# Revit family: Nuaire_IfcFanType_Svtc100
name_source: partatom
category: Mechanical Equipment
revit_build: Autodesk Revit 2018 (Build: 20170223_1515(x64)
units: mm (PartAtom-declared; Revit-internal decimal feet)

## family parameters
Always vertical = No
Cut with Voids When Loaded = No
OmniClass Number = 23.75.00.00
OmniClass Title = Climate Control (HVAC)
Part Type = Normal
Room Calculation Point = No
Round Connector Dimension = Use Diameter
Shared = No
Work Plane-Based = No

## types (4) — shared parameters
6 Monthly = SFG20 20-03
Access Clearance Left = 600 mm
Annually = SFG20 20-03
BMS Links = No
Battery Supply = No
CE Approval = Yes
COBie.Type = Yes
COBie.Type.Category = Pr_65_67_29_12 : Centrifugal fans
COBie.Type.Description = Car Park Impulse Fan
COBie.Type.DurationUnit = Year
COBie.Type.Length = 1916 mm  [stored 6.28609 ft]
COBie.Type.Manufacturer = Nuaire
COBie.Type.Material = Galvanised Steel
COBie.Type.NominalHeight = 320 mm  [stored 1.04987 ft]
COBie.Type.NominalLength = 1916 mm  [stored 6.28609 ft]
COBie.Type.NominalWidth = 1185 mm  [stored 3.8878 ft]
COBie.Type.WarrantyDescription = 3 Years.  1st year parts and labour, remaining 2 years parts only
COBie.Type.WarrantyDurationLabor = 1
COBie.Type.WarrantyDurationParts = 3
COBie.Type.WarrantyDurationUnit = Year
COBie.Type.WarrantyGuarantorLabor = Nuaire
COBie.Type.WarrantyGuarantorParts = Nuaire
Catalogue Pages = http://www.nuaire.info
Classification.Uniclass.Pr.Description = Pr_65_67_29_12
Classification.Uniclass.Pr.Number = Centrifugal fans
Daily = SFG20 20-03
Description = Car Park Impulse Fan
Enclosure Rating = Not Rated
Environmental Product Declaration = WEEE, RoHS
Fax Number = +44(0)2920-858-222
Fire Control Panel Links = No
Frequency = 50.00 Hz
Gross Weight = 165.00 kg
Height = 320 mm  [stored 1.04987 ft]
I&M Manual = http://nuaire.info
IFCExportAs = IfcFanType
IFCExportType = CENTRIFUGALBACKWARDINCLINEDCURVED
Length = 1916 mm  [stored 6.28609 ft]
Location of Manufacturer = 51.571856, -3.232638
Maintenance Required 0 to 300hrs = http://nuaire.info
Maintenance Required 1001 to 2000hrs = http://nuaire.info
Maintenance Required 2001 to 4000hrs = http://nuaire.info
Maintenance Required 301 to 600hrs = http://nuaire.info
Maintenance Required 4001 to 8000hrs = http://nuaire.info
Maintenance Required 601 to 1000hrs = http://nuaire.info
Maintenance Required 8001 to 12000hrs = http://nuaire.info
Manufacturer = Nuaire
Monthly = SFG20 20-03
Nominal Motor Rating = 2.200 kW
Nominal Motor Speed (rpm) = 1435
Number of Connection Poles = 3
Number of Motor Poles = 4
OmniClass Number = 23-33 31 19 13 15
OmniClass Title = Single Inlet Centrifugal Fans
Operation and Maintenance Manual = http://nuaire.info
Overall Length = 1966 mm  [stored 6.45013 ft]
Overall Width = 1254 mm  [stored 4.11417 ft]
Postcode = CF83 1NA
Power Source = Mains
Product Literature = http://www.nuaire.info
Product Range = SVTC
Quarterly = SFG20 20-03
Reference Standard = ISO 9001:2015
Responsible Sourcing of Materials = FSC
Revit Family Last Revised = 2021-09-28T09:40:00
Supply Phase = 3
Telephone Number = +44(0)2920-858-200
URL = http://www.nuaire.co.uk
Voltage = 400.00 V
Warranty Period = 3 Years
Weatherproof or Internal Only = Internal
Weekly = SFG20 20-03
Weight = 165.00 kg
Width = 1185 mm  [stored 3.8878 ft]
zero-valued in all types: COBie.Type.Area, COBie.Type.ReplacementCost, Life Cycle Analysis

## per-type parameters (varying)
| type | Apparent Load | COBie.Type.ModelNumber | COBie.Type.ModelReference | COBie.Type.Name | Full Load Current | Model | Starting Current | Temperature Rating |
| SVTC-100 | 2320 VA | SVCT-100 | SVCT-100 | SVCT-100 | 5.80 A | SVCT-100 | 30.16 A | 300°C for 2hrs |
| SVTC-100T8 | 2412 VA | SVTC-100T8 | SVTC-100T8 | SVTC-100T8 | 6.03 A | SVTC-100T8 | 30.20 A | 300°C for 2hrs |
| SVTC8-100T8 | 2412 VA | SVTC8-100T8 | SVTC8-100T8 | SVTC8-100T8 | 6.03 A | SVTC8-100T8 | 30.20 A | 400°C for 2hrs |
| SVTC8-100 | 2320 VA | SVTC8-100 | SVTC8-100 | SVTC8-100 | 5.80 A | SVTC8-100 | 30.16 A | 400°C for 2hrs |

note: [stored X ft] marks values corroborated as IEEE doubles in the binary element streams (Revit-internal decimal feet)

## geometry (parser evidence)
native form markers: Sweep x16
no freeform markers — native parametric forms only
